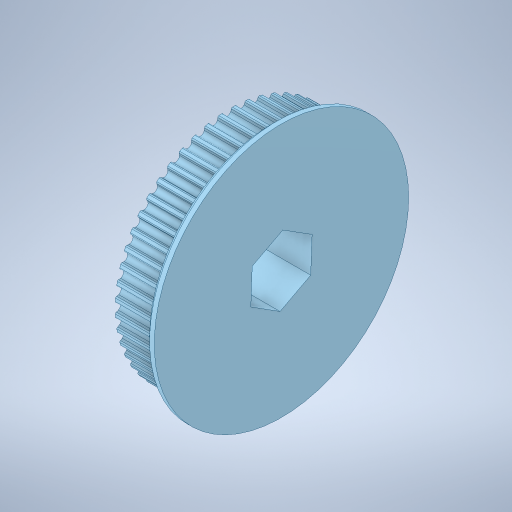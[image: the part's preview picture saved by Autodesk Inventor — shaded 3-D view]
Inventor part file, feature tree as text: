
AUTODESK INVENTOR PART (.ipt)
format: ipt  version: 2023.3 (Build 273359000, 359)  size: 739,328 bytes
history: native  units: in
note: dims shown in document units (in); Inventor stores cm internally (conversion verified against a paired STEP export)
features: other x1, extrude x1, pattern_circular x1, sketch x1
ambient origin geometry x8: Origin, YZ Plane, XZ Plane, XY Plane, X Axis, Y Axis, Z Axis, Center Point
bodies: Solid2 (feature_tree)
feature tree (4):
  other  "Part 1"
  extrude  "Extrusion2"  Depth=0.25in
  pattern_circular  "Circular Pattern1"  [2 undecoded]
  sketch  "Sketch2"  dims[d8=0.625in d9=0.2283in d10=0.25in d11=0.0in d12=1.5748in d13=360.0deg]
note: 2 required parameter values undecoded (feature->parameter linkage not recoverable at this tier; creation-order binding heuristic only, values carry confidence <= 0.55)
